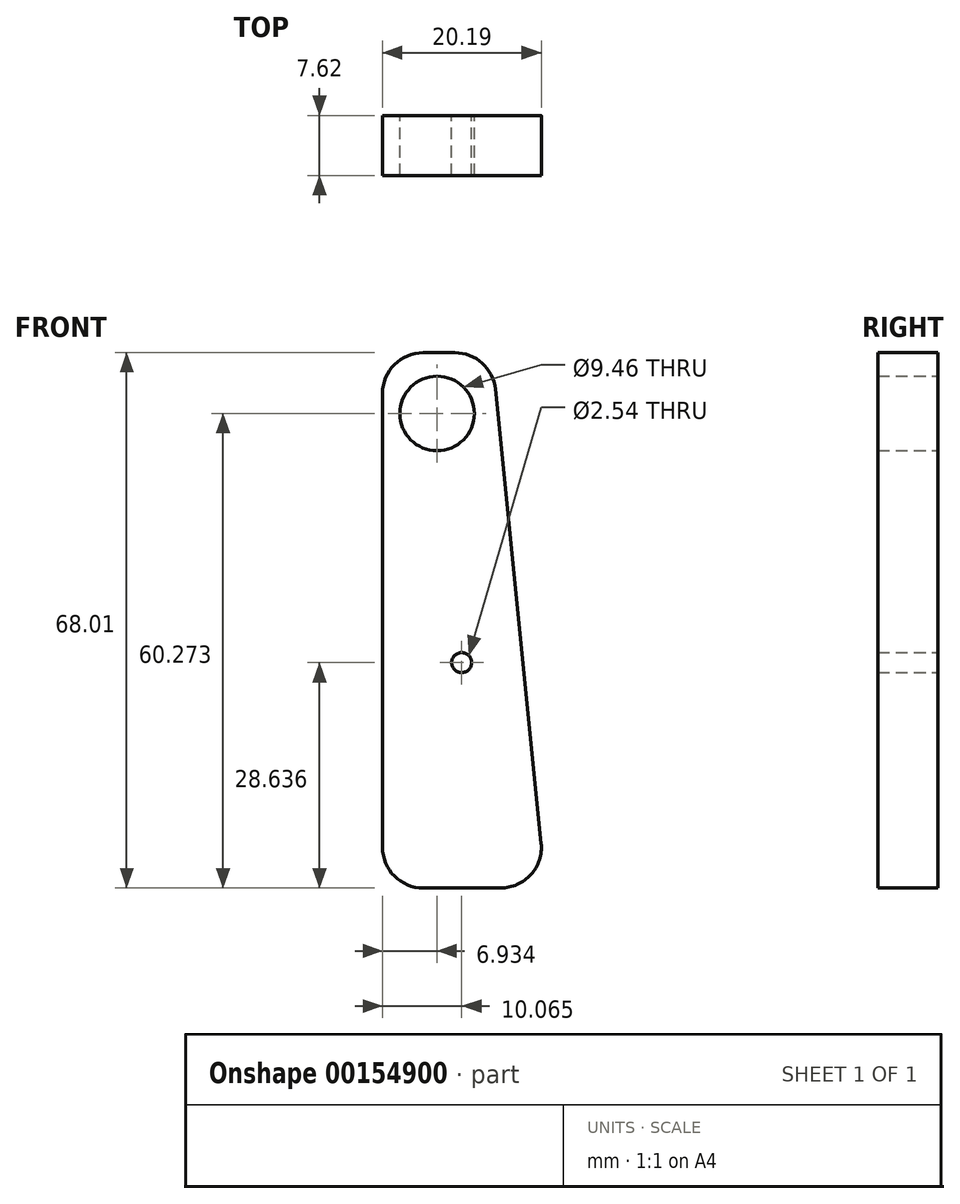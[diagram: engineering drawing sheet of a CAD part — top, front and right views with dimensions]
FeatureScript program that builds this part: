
annotation { "Feature Type Name" : "Feature", "Feature Type Description" : "" }
export const myFeature = defineFeature(function(context is Context, id is Id, definition is map)
    precondition{}
    {
        {
            var Q0;
            Q0=qCreatedBy(makeId("Front.planeOp"),FACE);
            var sketch = newSketch(context, id + "F0", { "sketchPlane" : qUnion([Q0])});
            skLineSegment(sketch, "E0", {"start": v(0, 56) * mm, "end": v(0, 0) * mm});
            skLineSegment(sketch, "E1", {"start": v(0, 0) * mm, "end": v(0, -12) * mm});
            skLineSegment(sketch, "E2", {"start": v(0, -12) * mm, "end": v(20.74, -12) * mm});
            skLineSegment(sketch, "E3", {"start": v(20.74, -12) * mm, "end": v(13.87, 56) * mm});
            skLineSegment(sketch, "E4", {"start": v(13.87, 56) * mm, "end": v(0, 56) * mm});
            skCircle(sketch, "E5", {"center": v(6.93, 48.27) * mm, "radius": 4.73 * mm});
            skPoint(sketch, "E5.centerSnap0", {"position": v(6.93, 56) * mm});
            skCircle(sketch, "E6", {"center": v(10.07, 16.64) * mm, "radius": 1.27 * mm});
            skSolve(sketch);
        }
        {
            var Q0;
            Q0=makeQuery(id+"F0.imprint","IMPRINT",FACE,{"disambiguationData":[TD([[makeQuery(id+"F0.imprint","IMPRINT",EDGE,{"derivedFrom":sQuery(id+"F0.wireOp",EDGE,"E0")}),1.0]])]});
            extrude(context, id + "F1", {"entities" : qUnion([Q0]), "depth" : 7.62 * mm});
        }
        {
            var Q0;
            Q0=makeQuery(id+"F1.opExtrude","SWEPT_EDGE",EDGE,{"disambiguationData":[OSD([sQuery(id+"F0.wireOp",EDGE,"E0"),sQuery(id+"F0.wireOp",EDGE,"E4")])]});
            var Q1;
            Q1=makeQuery(id+"F1.opExtrude","SWEPT_EDGE",EDGE,{"disambiguationData":[OSD([sQuery(id+"F0.wireOp",EDGE,"E3"),sQuery(id+"F0.wireOp",EDGE,"E4")])]});
            var Q2;
            Q2=makeQuery(id+"F1.opExtrude","SWEPT_EDGE",EDGE,{"disambiguationData":[OSD([sQuery(id+"F0.wireOp",EDGE,"E1"),sQuery(id+"F0.wireOp",EDGE,"E2")])]});
            var Q3;
            Q3=makeQuery(id+"F1.opExtrude","SWEPT_EDGE",EDGE,{"disambiguationData":[OSD([sQuery(id+"F0.wireOp",EDGE,"E2"),sQuery(id+"F0.wireOp",EDGE,"E3")])]});
            fillet(context, id + "F2", {"entities" : qUnion([Q0, Q1, Q2, Q3]), "radius" : 5.17 * mm, "tangentPropagation" : true, "allowEdgeOverflow" : false});
        }
    });
